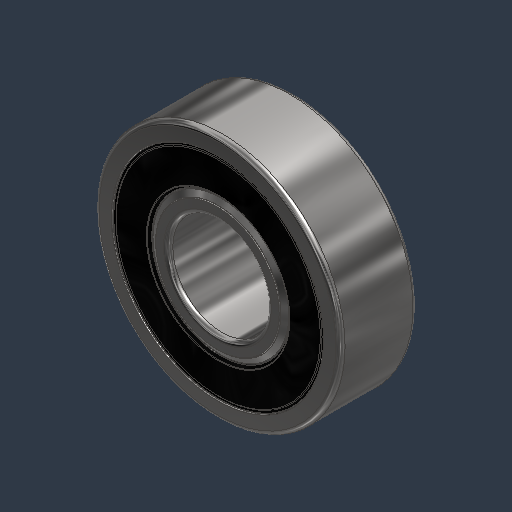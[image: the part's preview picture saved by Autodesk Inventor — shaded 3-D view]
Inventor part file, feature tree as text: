
AUTODESK INVENTOR PART (.ipt)
format: ipt  version: 2024.3 (Build 283343000, 343)  size: 2,516,480 bytes
history: native  units: mm (DEFAULTED — no unit token found)
features: other x14, fillet x4, mirror x2, pattern_circular x1, revolve x1
ambient origin geometry x8: Origin, YZ Plane, XZ Plane, XY Plane, X Axis, Y Axis, Z Axis, Center Point
bodies: Solid1 (feature_tree), Solid2 (feature_tree), Solid3 (feature_tree), Solid4 (feature_tree), Solid5 (feature_tree), Solid6 (feature_tree), Solid7 (feature_tree), Solid8 (feature_tree), Solid9 (feature_tree), Solid10 (feature_tree), Solid11 (feature_tree), Solid12 (feature_tree), Solid13 (feature_tree), Solid14 (feature_tree), Solid15 (feature_tree), Solid16 (feature_tree), Solid17 (feature_tree), Solid18 (feature_tree), Solid19 (feature_tree), Solid20 (feature_tree), Solid21 (feature_tree), Solid22 (feature_tree)
feature tree (22):
  pattern_circular  "CirPattern2"
  mirror  "Mirror1"
  fillet  "Fillet2"  [1 undecoded]
  other  "CirPattern3[1]"
  other  "CirPattern3[2]"
  other  "CirPattern3[3]"
  other  "CirPattern3[4]"
  other  "CirPattern3[5]"
  other  "CirPattern3[6]"
  revolve  "Revolve4"  [1 undecoded]
  other  "CirPattern4[1]"
  other  "CirPattern4[2]"
  other  "CirPattern4[3]"
  other  "CirPattern4[4]"
  other  "CirPattern4[5]"
  other  "CirPattern4[6]"
  other  "CirPattern3[7]"
  other  "CirPattern4[7]"
  fillet  "Fillet5"  [1 undecoded]
  fillet  "Fillet7"  [1 undecoded]
  mirror  "Mirror2"
  fillet  "Fillet6"  [1 undecoded]
note: 5 required parameter values undecoded (feature->parameter linkage not recoverable at this tier; creation-order binding heuristic only, values carry confidence <= 0.55)
